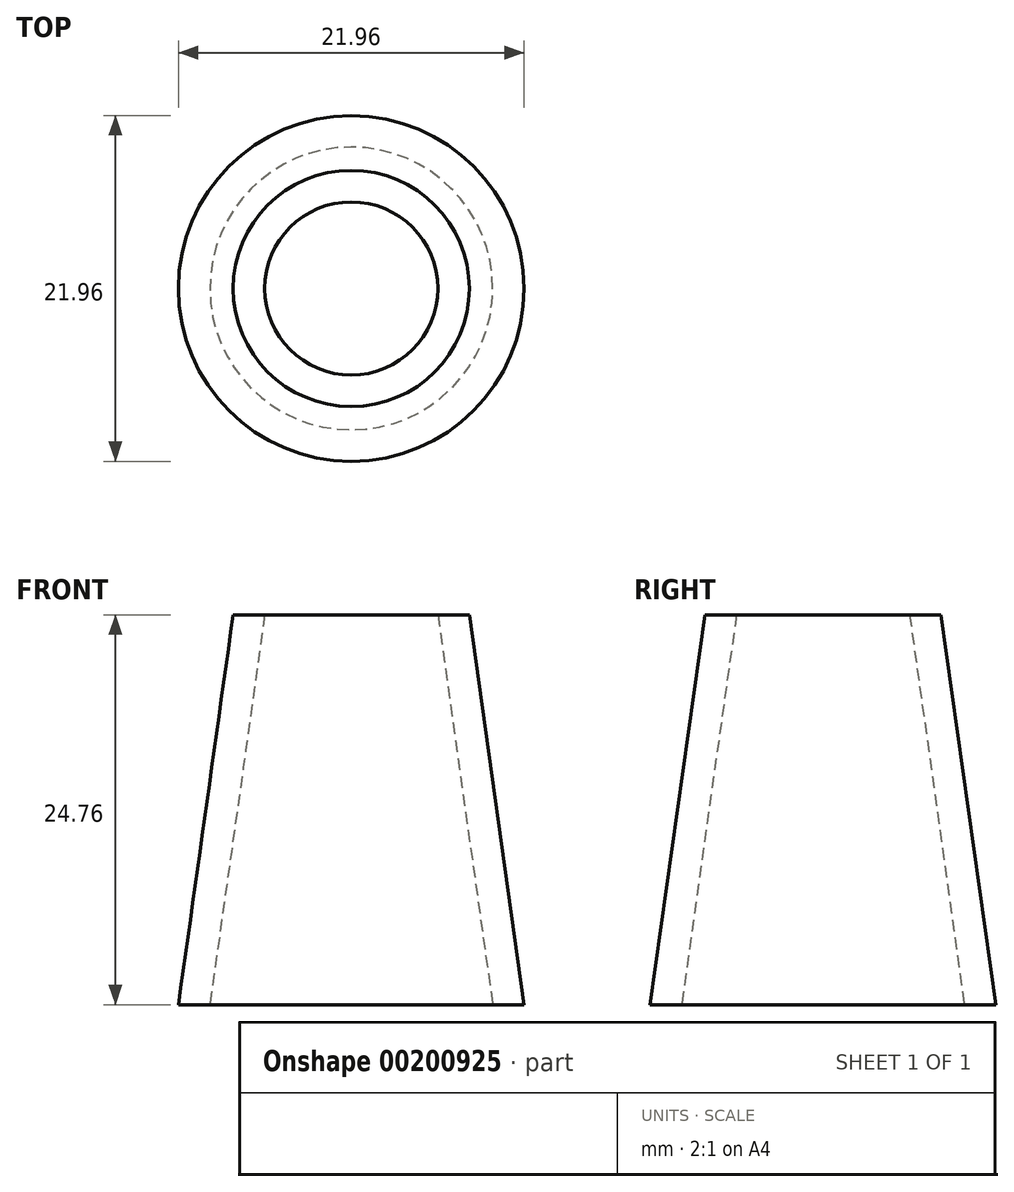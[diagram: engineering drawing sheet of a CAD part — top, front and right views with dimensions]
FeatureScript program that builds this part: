
annotation { "Feature Type Name" : "Feature", "Feature Type Description" : "" }
export const myFeature = defineFeature(function(context is Context, id is Id, definition is map)
    precondition{}
    {
        {
            var Q0;
            Q0=qCreatedBy(makeId("Front.planeOp"),FACE);
            var sketch = newSketch(context, id + "F0", { "sketchPlane" : qUnion([Q0])});
            skLineSegment(sketch, "E0.bottom", {"start": v(-8.6, 28.59) * mm, "end": v(-19.86, 28.59) * mm});
            skLineSegment(sketch, "E0.top", {"start": v(-8.6, 39.86) * mm, "end": v(-19.86, 39.86) * mm});
            skLineSegment(sketch, "E0.left", {"start": v(-8.6, 28.59) * mm, "end": v(-8.6, 39.86) * mm});
            skLineSegment(sketch, "E0.right", {"start": v(-19.86, 28.59) * mm, "end": v(-19.86, 39.86) * mm});
            skLineSegment(sketch, "E1", {"start": v(16.9, 24.76) * mm, "end": v(13.42, 0) * mm});
            skLineSegment(sketch, "E2", {"start": v(16.9, 24.76) * mm, "end": v(18.9, 24.76) * mm});
            skLineSegment(sketch, "E3", {"start": v(18.9, 24.76) * mm, "end": v(15.42, 0) * mm});
            skLineSegment(sketch, "E4", {"start": v(15.42, 0) * mm, "end": v(13.42, 0) * mm});
            skSolve(sketch);
        }
        {
            var Q0;
            Q0=makeQuery(id+"F0.imprint","IMPRINT",FACE,{"disambiguationData":[TD([[makeQuery(id+"F0.imprint","IMPRINT",EDGE,{"derivedFrom":sQuery(id+"F0.wireOp",EDGE,"E1")}),1.0]])]});
            var sketch = newSketch(context, id + "F1", { "sketchPlane" : qUnion([Q0])});
            skLineSegment(sketch, "E5", {"start": v(24.4, 0) * mm, "end": v(24.4, 56.32) * mm});
            skSolve(sketch);
        }
        {
            var Q0;
            Q0=makeQuery(id+"F0.imprint","IMPRINT",FACE,{"disambiguationData":[TD([[makeQuery(id+"F0.imprint","IMPRINT",EDGE,{"derivedFrom":sQuery(id+"F0.wireOp",EDGE,"E1")}),1.0]])]});
            var Q1;
            Q1=sQuery(id+"F1.wireOp",EDGE,"E5");
            revolve(context, id + "F2", {"entities" : qUnion([Q0]), "axis" : qUnion([Q1]), "revolveType" : RevolveType.FULL});
        }
    });
